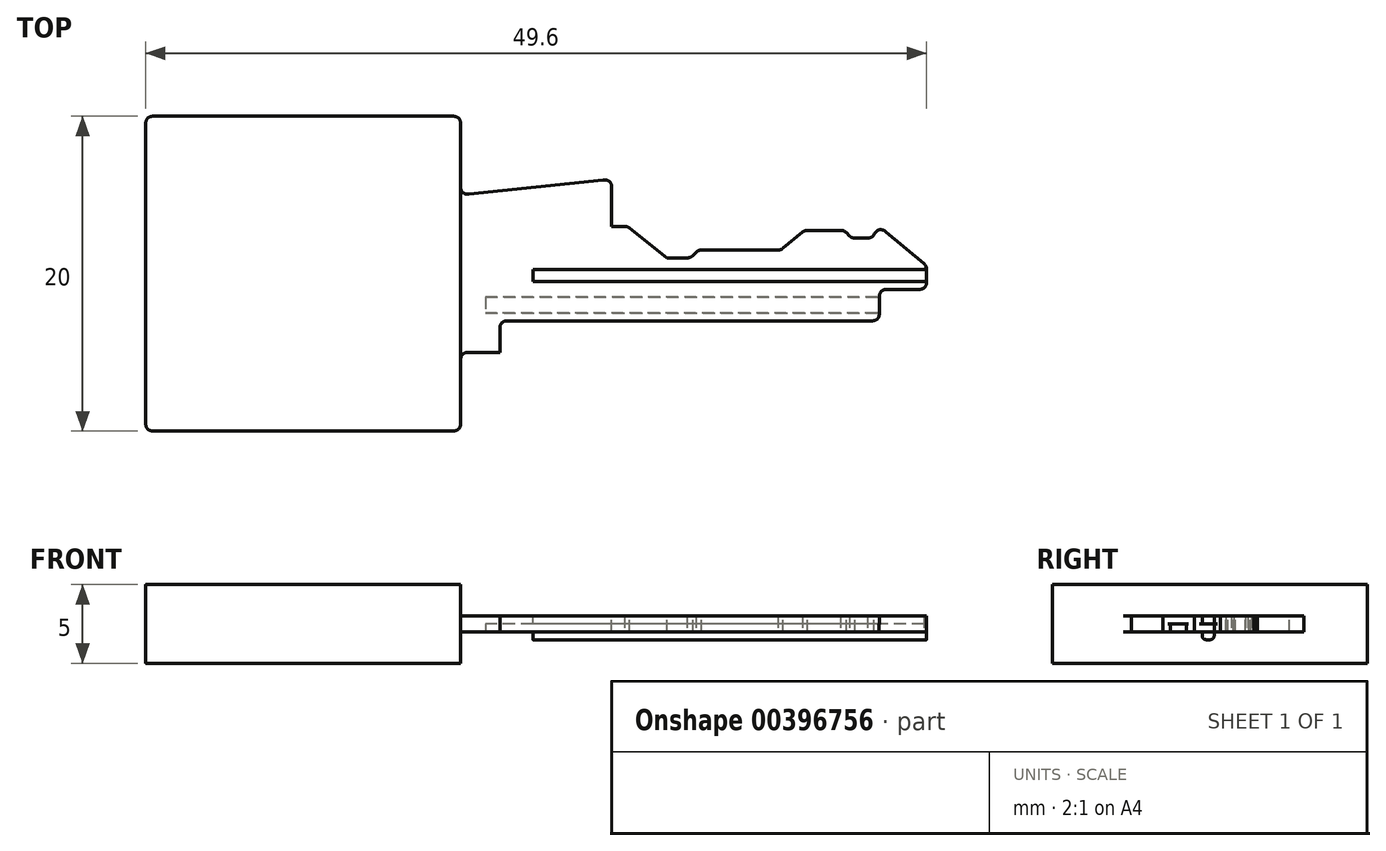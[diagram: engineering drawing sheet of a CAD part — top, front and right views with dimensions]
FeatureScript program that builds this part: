
annotation { "Feature Type Name" : "Feature", "Feature Type Description" : "" }
export const myFeature = defineFeature(function(context is Context, id is Id, definition is map)
    precondition{}
    {
        {
            var Q0;
            Q0=qCreatedBy(makeId("Top.planeOp"),FACE);
            var sketch = newSketch(context, id + "F0", { "sketchPlane" : qUnion([Q0])});
            skLineSegment(sketch, "E0.bottom", {"start": v(0, 0) * mm, "end": v(-20, 0) * mm});
            skLineSegment(sketch, "E0.top", {"start": v(0, 20) * mm, "end": v(-20, 20) * mm});
            skLineSegment(sketch, "E0.left", {"start": v(0, 0) * mm, "end": v(0, 20) * mm});
            skLineSegment(sketch, "E0.right", {"start": v(-20, 0) * mm, "end": v(-20, 20) * mm});
            skLineSegment(sketch, "E1", {"start": v(0, 15) * mm, "end": v(10, 15) * mm});
            skLineSegment(sketch, "E2", {"start": v(10, 15) * mm, "end": v(10, 5) * mm});
            skLineSegment(sketch, "E3", {"start": v(10, 5) * mm, "end": v(0, 5) * mm});
            skLineSegment(sketch, "E4", {"start": v(0, 5) * mm, "end": v(0, 15) * mm});
            skLineSegment(sketch, "E5.bottom", {"start": v(10, 15) * mm, "end": v(39, 15) * mm});
            skLineSegment(sketch, "E5.top", {"start": v(10, 5) * mm, "end": v(39, 5) * mm});
            skLineSegment(sketch, "E5.right", {"start": v(39, 15) * mm, "end": v(39, 5) * mm});
            skSolve(sketch);
        }
        {
            var Q0;
            {var subQ3=sQuery(id+"F0.wireOp",EDGE,"E0.bottom");Q0=makeQuery(id+"F0.imprint","IMPRINT",FACE,{"disambiguationData":[TD([[makeQuery(id+"F0.imprint","IMPRINT",EDGE,{"derivedFrom":subQ3}),-1.0]])]});}
            var Q1;
            Q1=makeQuery(id+"F0.imprint","IMPRINT",FACE,{"disambiguationData":[TD([[makeQuery(id+"F0.imprint","IMPRINT",EDGE,{"derivedFrom":sQuery(id+"F0.wireOp",EDGE,"E1")}),-1.0]])]});
            var Q2;
            Q2=makeQuery(id+"F0.imprint","IMPRINT",FACE,{"disambiguationData":[TD([[makeQuery(id+"F0.imprint","IMPRINT",EDGE,{"derivedFrom":sQuery(id+"F0.wireOp",EDGE,"E5.bottom")}),-1.0]])]});
            extrude(context, id + "F1", {"entities" : qUnion([Q0, Q1, Q2]), "depth" : 1 * mm});
        }
        {
            var Q0;
            Q0=makeQuery(id+"F1.opExtrude","CAP_FACE",FACE,{"disambiguationData":[OSD([sQuery(id+"F0.wireOp",EDGE,"E0.bottom"),sQuery(id+"F0.wireOp",EDGE,"E0.top"),sQuery(id+"F0.wireOp",EDGE,"E0.left"),sQuery(id+"F0.wireOp",EDGE,"E0.right"),sQuery(id+"F0.wireOp",EDGE,"E1"),sQuery(id+"F0.wireOp",EDGE,"E3"),sQuery(id+"F0.wireOp",EDGE,"E5.bottom"),sQuery(id+"F0.wireOp",EDGE,"E5.top"),sQuery(id+"F0.wireOp",EDGE,"E5.right")])],"isStart":false});
            var sketch = newSketch(context, id + "F2", { "sketchPlane" : qUnion([Q0])});
            skLineSegment(sketch, "E6", {"start": v(0, 15) * mm, "end": v(9.6, 15) * mm});
            skLineSegment(sketch, "E7", {"start": v(9.6, 15) * mm, "end": v(9.6, 16) * mm});
            skLineSegment(sketch, "E8", {"start": v(9.6, 16) * mm, "end": v(0, 15) * mm});
            skSolve(sketch);
        }
        {
            var Q0;
            Q0=makeQuery(id+"F2.imprint","IMPRINT",FACE,{"disambiguationData":[TD([[makeQuery(id+"F2.imprint","IMPRINT",EDGE,{"derivedFrom":sQuery(id+"F2.wireOp",EDGE,"E6")}),1.0]])]});
            extrude(context, id + "F3", {"entities" : qUnion([Q0]), "operationType" : NewBodyOperationType.ADD, "oppositeDirection" : true, "depth" : 1 * mm});
        }
        {
            var Q0;
            Q0=makeQuery(id+"F3.boolean.opBoolean","MERGE",FACE,{"derivedFrom":[makeQuery(id+"F1.opExtrude","CAP_FACE",FACE,{"disambiguationData":[OSD([sQuery(id+"F0.wireOp",EDGE,"E0.bottom"),sQuery(id+"F0.wireOp",EDGE,"E0.top"),sQuery(id+"F0.wireOp",EDGE,"E0.left"),sQuery(id+"F0.wireOp",EDGE,"E0.right"),sQuery(id+"F0.wireOp",EDGE,"E1"),sQuery(id+"F0.wireOp",EDGE,"E3"),sQuery(id+"F0.wireOp",EDGE,"E5.bottom"),sQuery(id+"F0.wireOp",EDGE,"E5.top"),sQuery(id+"F0.wireOp",EDGE,"E5.right")])],"isStart":false}),makeQuery(id+"F3.opExtrude","CAP_FACE",FACE,{"disambiguationData":[OSD([sQuery(id+"F2.wireOp",EDGE,"E6"),sQuery(id+"F2.wireOp",EDGE,"E7"),sQuery(id+"F2.wireOp",EDGE,"E8")])],"isStart":true})]});
            var sketch = newSketch(context, id + "F4", { "sketchPlane" : qUnion([Q0])});
            skLineSegment(sketch, "E9", {"start": v(9.6, 15) * mm, "end": v(9.6, 13) * mm});
            skLineSegment(sketch, "E10", {"start": v(9.6, 13) * mm, "end": v(10.6, 13) * mm});
            skLineSegment(sketch, "E11", {"start": v(10.6, 13) * mm, "end": v(13.1, 11) * mm});
            skLineSegment(sketch, "E12", {"start": v(13.1, 11) * mm, "end": v(14.6, 11) * mm});
            skLineSegment(sketch, "E13", {"start": v(14.6, 11) * mm, "end": v(15.1, 11.5) * mm});
            skLineSegment(sketch, "E14", {"start": v(15.1, 11.5) * mm, "end": v(20.35, 11.5) * mm});
            skLineSegment(sketch, "E15", {"start": v(20.35, 11.5) * mm, "end": v(21.85, 12.75) * mm});
            skLineSegment(sketch, "E16", {"start": v(21.85, 12.75) * mm, "end": v(24.35, 12.75) * mm});
            skLineSegment(sketch, "E17", {"start": v(24.35, 12.75) * mm, "end": v(24.85, 12.25) * mm});
            skLineSegment(sketch, "E18", {"start": v(24.85, 12.25) * mm, "end": v(26.1, 12.25) * mm});
            skLineSegment(sketch, "E19", {"start": v(26.1, 12.25) * mm, "end": v(26.6, 13) * mm});
            skLineSegment(sketch, "E20", {"start": v(26.6, 13) * mm, "end": v(29.6, 10.5) * mm});
            skLineSegment(sketch, "E21", {"start": v(29.6, 10.5) * mm, "end": v(29.6, 9) * mm});
            skLineSegment(sketch, "E22", {"start": v(29.6, 9) * mm, "end": v(26.6, 9) * mm});
            skLineSegment(sketch, "E23", {"start": v(26.6, 9) * mm, "end": v(26.6, 7) * mm});
            skLineSegment(sketch, "E24", {"start": v(26.6, 7) * mm, "end": v(2.5, 7) * mm});
            skLineSegment(sketch, "E25", {"start": v(2.5, 7) * mm, "end": v(2.5, 5) * mm});
            skLineSegment(sketch, "E26", {"start": v(2.5, 5) * mm, "end": v(39, 5) * mm});
            skLineSegment(sketch, "E27", {"start": v(39, 5) * mm, "end": v(39, 15) * mm});
            skLineSegment(sketch, "E28", {"start": v(39, 15) * mm, "end": v(9.6, 15) * mm});
            skSolve(sketch);
        }
        {
            var Q0;
            Q0=makeQuery(id+"F4.imprint","IMPRINT",FACE,{"disambiguationData":[TD([[makeQuery(id+"F4.imprint","IMPRINT",EDGE,{"derivedFrom":sQuery(id+"F4.wireOp",EDGE,"E9")}),1.0]])]});
            extrude(context, id + "F5", {"entities" : qUnion([Q0]), "operationType" : NewBodyOperationType.REMOVE, "oppositeDirection" : true, "depth" : 1 * mm});
        }
        {
            var Q0;
            Q0=makeQuery(id+"F3.opExtrude","SWEPT_EDGE",EDGE,{"disambiguationData":[OSD([sQuery(id+"F2.wireOp",EDGE,"E7"),sQuery(id+"F2.wireOp",EDGE,"E8")])]});
            var Q1;
            Q1=makeQuery(id+"F5.boolean.opBoolean","COPY",EDGE,{"derivedFrom":makeQuery(id+"F5.opExtrude","SWEPT_EDGE",EDGE,{"disambiguationData":[OSD([sQuery(id+"F4.wireOp",EDGE,"E10"),sQuery(id+"F4.wireOp",EDGE,"E11")])]})});
            var Q2;
            Q2=makeQuery(id+"F5.boolean.opBoolean","COPY",EDGE,{"derivedFrom":makeQuery(id+"F5.opExtrude","SWEPT_EDGE",EDGE,{"disambiguationData":[OSD([sQuery(id+"F4.wireOp",EDGE,"E12"),sQuery(id+"F4.wireOp",EDGE,"E13")])]})});
            var Q3;
            Q3=makeQuery(id+"F5.boolean.opBoolean","COPY",EDGE,{"derivedFrom":makeQuery(id+"F5.opExtrude","SWEPT_EDGE",EDGE,{"disambiguationData":[OSD([sQuery(id+"F4.wireOp",EDGE,"E14"),sQuery(id+"F4.wireOp",EDGE,"E15")])]})});
            var Q4;
            Q4=makeQuery(id+"F5.boolean.opBoolean","COPY",EDGE,{"derivedFrom":makeQuery(id+"F5.opExtrude","SWEPT_EDGE",EDGE,{"disambiguationData":[OSD([sQuery(id+"F4.wireOp",EDGE,"E15"),sQuery(id+"F4.wireOp",EDGE,"E16")])]})});
            var Q5;
            Q5=makeQuery(id+"F5.boolean.opBoolean","COPY",EDGE,{"derivedFrom":makeQuery(id+"F5.opExtrude","SWEPT_EDGE",EDGE,{"disambiguationData":[OSD([sQuery(id+"F4.wireOp",EDGE,"E16"),sQuery(id+"F4.wireOp",EDGE,"E17")])]})});
            var Q6;
            Q6=makeQuery(id+"F5.boolean.opBoolean","COPY",EDGE,{"derivedFrom":makeQuery(id+"F5.opExtrude","SWEPT_EDGE",EDGE,{"disambiguationData":[OSD([sQuery(id+"F4.wireOp",EDGE,"E17"),sQuery(id+"F4.wireOp",EDGE,"E18")])]})});
            var Q7;
            Q7=makeQuery(id+"F5.boolean.opBoolean","COPY",EDGE,{"derivedFrom":makeQuery(id+"F5.opExtrude","SWEPT_EDGE",EDGE,{"disambiguationData":[OSD([sQuery(id+"F4.wireOp",EDGE,"E18"),sQuery(id+"F4.wireOp",EDGE,"E19")])]})});
            var Q8;
            Q8=makeQuery(id+"F5.boolean.opBoolean","COPY",EDGE,{"derivedFrom":makeQuery(id+"F5.opExtrude","SWEPT_EDGE",EDGE,{"disambiguationData":[OSD([sQuery(id+"F4.wireOp",EDGE,"E21"),sQuery(id+"F4.wireOp",EDGE,"E22")])]})});
            var Q9;
            Q9=makeQuery(id+"F5.boolean.opBoolean","COPY",EDGE,{"derivedFrom":makeQuery(id+"F5.opExtrude","SWEPT_EDGE",EDGE,{"disambiguationData":[OSD([sQuery(id+"F4.wireOp",EDGE,"E20"),sQuery(id+"F4.wireOp",EDGE,"E21")])]})});
            var Q10;
            Q10=makeQuery(id+"F5.boolean.opBoolean","COPY",EDGE,{"derivedFrom":makeQuery(id+"F5.opExtrude","SWEPT_EDGE",EDGE,{"disambiguationData":[OSD([sQuery(id+"F4.wireOp",EDGE,"E19"),sQuery(id+"F4.wireOp",EDGE,"E20")])]})});
            var Q11;
            Q11=makeQuery(id+"F5.boolean.opBoolean","COPY",EDGE,{"derivedFrom":makeQuery(id+"F5.opExtrude","SWEPT_EDGE",EDGE,{"disambiguationData":[OSD([sQuery(id+"F4.wireOp",EDGE,"E22"),sQuery(id+"F4.wireOp",EDGE,"E23")])]})});
            var Q12;
            Q12=makeQuery(id+"F5.boolean.opBoolean","COPY",EDGE,{"derivedFrom":makeQuery(id+"F5.opExtrude","SWEPT_EDGE",EDGE,{"disambiguationData":[OSD([sQuery(id+"F4.wireOp",EDGE,"E23"),sQuery(id+"F4.wireOp",EDGE,"E24")])]})});
            var Q13;
            Q13=makeQuery(id+"F5.boolean.opBoolean","COPY",EDGE,{"derivedFrom":makeQuery(id+"F5.opExtrude","SWEPT_EDGE",EDGE,{"disambiguationData":[OSD([sQuery(id+"F4.wireOp",EDGE,"E24"),sQuery(id+"F4.wireOp",EDGE,"E25")])]})});
            var Q14;
            Q14=makeQuery(id+"F5.boolean.opBoolean","COPY",EDGE,{"derivedFrom":makeQuery(id+"F5.opExtrude","SWEPT_EDGE",EDGE,{"disambiguationData":[OSD([sQuery(id+"F0.wireOp",EDGE,"E3"),sQuery(id+"F0.wireOp",EDGE,"E5.top"),sQuery(id+"F4.wireOp",EDGE,"E25"),sQuery(id+"F4.wireOp",EDGE,"E26")])]})});
            var Q15;
            Q15=makeQuery(id+"F1.opExtrude","SWEPT_EDGE",EDGE,{"disambiguationData":[OSD([sQuery(id+"F0.wireOp",EDGE,"E0.left"),sQuery(id+"F0.wireOp",EDGE,"E3"),sQuery(id+"F0.wireOp",EDGE,"E4")])]});
            var Q16;
            Q16=makeQuery(id+"F1.opExtrude","SWEPT_EDGE",EDGE,{"disambiguationData":[OSD([sQuery(id+"F0.wireOp",EDGE,"E0.bottom"),sQuery(id+"F0.wireOp",EDGE,"E0.left")])]});
            var Q17;
            Q17=makeQuery(id+"F1.opExtrude","SWEPT_EDGE",EDGE,{"disambiguationData":[OSD([sQuery(id+"F0.wireOp",EDGE,"E0.top"),sQuery(id+"F0.wireOp",EDGE,"E0.left")])]});
            var Q18;
            {var subQ0=sQuery(id+"F0.wireOp",EDGE,"E0.left");Q18=makeQuery(id+"F3.boolean.opBoolean","MERGE",EDGE,{"derivedFrom":[makeQuery(id+"F1.opExtrude","SWEPT_EDGE",EDGE,{"disambiguationData":[OSD([subQ0,sQuery(id+"F0.wireOp",EDGE,"E1"),sQuery(id+"F0.wireOp",EDGE,"E4")])]}),makeQuery(id+"F3.opExtrude","SWEPT_EDGE",EDGE,{"disambiguationData":[OSD([subQ0,sQuery(id+"F2.wireOp",EDGE,"E6"),sQuery(id+"F2.wireOp",EDGE,"E8")])]})]});}
            var Q19;
            Q19=makeQuery(id+"F1.opExtrude","SWEPT_EDGE",EDGE,{"disambiguationData":[OSD([sQuery(id+"F0.wireOp",EDGE,"E0.top"),sQuery(id+"F0.wireOp",EDGE,"E0.right")])]});
            var Q20;
            Q20=makeQuery(id+"F1.opExtrude","SWEPT_EDGE",EDGE,{"disambiguationData":[OSD([sQuery(id+"F0.wireOp",EDGE,"E0.bottom"),sQuery(id+"F0.wireOp",EDGE,"E0.right")])]});
            var Q21;
            Q21=makeQuery(id+"F5.boolean.opBoolean","COPY",EDGE,{"derivedFrom":makeQuery(id+"F5.opExtrude","SWEPT_EDGE",EDGE,{"disambiguationData":[OSD([sQuery(id+"F4.wireOp",EDGE,"E13"),sQuery(id+"F4.wireOp",EDGE,"E14")])]})});
            fillet(context, id + "F6", {"entities" : qUnion([Q0, Q1, Q2, Q3, Q4, Q5, Q6, Q7, Q8, Q9, Q10, Q11, Q12, Q13, Q14, Q15, Q16, Q17, Q18, Q19, Q20, Q21]), "radius" : .5 * mm, "tangentPropagation" : true, "rho" : 0.5, "crossSection" : FilletCrossSection.CONIC, "allowEdgeOverflow" : false});
        }
        {
            var Q0;
            Q0=makeQuery(id+"F5.boolean.opBoolean","COPY",FACE,{"derivedFrom":makeQuery(id+"F5.opExtrude","SWEPT_FACE",FACE,{"disambiguationData":[OSD([sQuery(id+"F4.wireOp",EDGE,"E23")])]})});
            var sketch = newSketch(context, id + "F7", { "sketchPlane" : qUnion([Q0])});
            skLineSegment(sketch, "E29", {"start": v(9, 0) * mm, "end": v(9, 0.5) * mm});
            skLineSegment(sketch, "E30", {"start": v(9, 0.5) * mm, "end": v(7.5, 0.5) * mm});
            skLineSegment(sketch, "E31", {"start": v(7.5, 0.5) * mm, "end": v(7.5, 0) * mm});
            skLineSegment(sketch, "E32", {"start": v(7.5, 0) * mm, "end": v(9, 0) * mm});
            skLineSegment(sketch, "E33", {"start": v(9, 0.5) * mm, "end": v(9, 0) * mm});
            skLineSegment(sketch, "E34", {"start": v(7.5, 1) * mm, "end": v(7.5, 1.5) * mm});
            skLineSegment(sketch, "E35", {"start": v(7.5, 1.5) * mm, "end": v(9, 1.5) * mm});
            skLineSegment(sketch, "E36", {"start": v(9, 1.5) * mm, "end": v(9, 1) * mm});
            skLineSegment(sketch, "E37", {"start": v(9, 1) * mm, "end": v(7.5, 1) * mm});
            skSolve(sketch);
        }
        {
            var Q0;
            {var subQ0=sQuery(id+"F7.wireOp",EDGE,"E31");Q0=makeQuery(id+"F7.imprint","IMPRINT",FACE,{"disambiguationData":[TD([[makeQuery(id+"F7.imprint","IMPRINT",EDGE,{"derivedFrom":subQ0}),1.0]])]});}
            extrude(context, id + "F8", {"entities" : qUnion([Q0]), "operationType" : NewBodyOperationType.REMOVE, "oppositeDirection" : true, "depth" : 25 * mm});
        }
        {
            var Q0;
            {var subQ0=sQuery(id+"F4.wireOp",EDGE,"E23");Q0=makeQuery(id+"F8.boolean.opBoolean","MERGE",EDGE,{"derivedFrom":[makeQuery(id+"F6.opFillet","BLEND_EDGE",EDGE,{"blendedFrom":[makeQuery(id+"F5.boolean.opBoolean","COPY",EDGE,{"derivedFrom":makeQuery(id+"F5.opExtrude","SWEPT_EDGE",EDGE,{"disambiguationData":[OSD([subQ0,sQuery(id+"F4.wireOp",EDGE,"E24")])]})}),makeQuery(id+"F5.boolean.opBoolean","COPY",FACE,{"derivedFrom":makeQuery(id+"F5.opExtrude","SWEPT_FACE",FACE,{"disambiguationData":[OSD([subQ0])]})})],"blendedInto":[makeQuery(id+"F5.boolean.opBoolean","COPY",FACE,{"derivedFrom":makeQuery(id+"F5.opExtrude","SWEPT_FACE",FACE,{"disambiguationData":[OSD([subQ0])]})})]}),makeQuery(id+"F8.opExtrude","CAP_EDGE",EDGE,{"disambiguationData":[OSD([sQuery(id+"F7.wireOp",EDGE,"E31")])],"isStart":true})]});}
            var Q1;
            {var subQ0=sQuery(id+"F4.wireOp",EDGE,"E23");var subQ1=sQuery(id+"F4.wireOp",EDGE,"E22");Q1=makeQuery(id+"F8.boolean.opBoolean","MERGE",EDGE,{"derivedFrom":[makeQuery(id+"F6.opFillet","BLEND_EDGE",EDGE,{"blendedFrom":[makeQuery(id+"F5.boolean.opBoolean","COPY",EDGE,{"derivedFrom":makeQuery(id+"F5.opExtrude","SWEPT_EDGE",EDGE,{"disambiguationData":[OSD([subQ1,subQ0])]})}),makeQuery(id+"F5.boolean.opBoolean","COPY",FACE,{"derivedFrom":makeQuery(id+"F5.opExtrude","SWEPT_FACE",FACE,{"disambiguationData":[OSD([subQ0])]})})],"blendedInto":[makeQuery(id+"F5.boolean.opBoolean","COPY",FACE,{"derivedFrom":makeQuery(id+"F5.opExtrude","SWEPT_FACE",FACE,{"disambiguationData":[OSD([subQ0])]})})]}),makeQuery(id+"F8.opExtrude","CAP_EDGE",EDGE,{"disambiguationData":[OSD([subQ1,subQ0])],"isStart":true})]});}
            fillet(context, id + "F9", {"entities" : qUnion([Q0, Q1]), "radius" : 0.15 * mm, "tangentPropagation" : true, "allowEdgeOverflow" : false});
        }
        {
            var Q0;
            Q0=makeQuery(id+"F5.boolean.opBoolean","COPY",FACE,{"derivedFrom":makeQuery(id+"F5.opExtrude","SWEPT_FACE",FACE,{"disambiguationData":[OSD([sQuery(id+"F4.wireOp",EDGE,"E21")])]})});
            var sketch = newSketch(context, id + "F10", { "sketchPlane" : qUnion([Q0])});
            skLineSegment(sketch, "E38", {"start": v(9.5, 1) * mm, "end": v(9.5, 0.5) * mm});
            skLineSegment(sketch, "E39", {"start": v(9.5, 0.5) * mm, "end": v(10.27, 0.5) * mm});
            skLineSegment(sketch, "E40", {"start": v(10.27, 0.5) * mm, "end": v(10.27, 1) * mm});
            skLineSegment(sketch, "E41", {"start": v(10.27, 1) * mm, "end": v(9.5, 1) * mm});
            skSolve(sketch);
        }
        {
            var Q0;
            Q0=makeQuery(id+"F10.imprint","IMPRINT",FACE,{"disambiguationData":[TD([[makeQuery(id+"F10.imprint","IMPRINT",EDGE,{"derivedFrom":sQuery(id+"F10.wireOp",EDGE,"E38")}),1.0]])]});
            extrude(context, id + "F11", {"entities" : qUnion([Q0]), "operationType" : NewBodyOperationType.REMOVE, "oppositeDirection" : true, "depth" : 25 * mm});
        }
        {
            var Q0;
            {var subQ0=sQuery(id+"F4.wireOp",EDGE,"E21");Q0=makeQuery(id+"F11.boolean.opBoolean","MERGE",EDGE,{"derivedFrom":[makeQuery(id+"F6.opFillet","BLEND_EDGE",EDGE,{"blendedFrom":[makeQuery(id+"F5.boolean.opBoolean","COPY",EDGE,{"derivedFrom":makeQuery(id+"F5.opExtrude","SWEPT_EDGE",EDGE,{"disambiguationData":[OSD([subQ0,sQuery(id+"F4.wireOp",EDGE,"E22")])]})}),makeQuery(id+"F5.boolean.opBoolean","COPY",FACE,{"derivedFrom":makeQuery(id+"F5.opExtrude","SWEPT_FACE",FACE,{"disambiguationData":[OSD([subQ0])]})})],"blendedInto":[makeQuery(id+"F5.boolean.opBoolean","COPY",FACE,{"derivedFrom":makeQuery(id+"F5.opExtrude","SWEPT_FACE",FACE,{"disambiguationData":[OSD([subQ0])]})})]}),makeQuery(id+"F11.opExtrude","CAP_EDGE",EDGE,{"disambiguationData":[OSD([sQuery(id+"F10.wireOp",EDGE,"E38")])],"isStart":true})]});}
            var Q1;
            {var subQ0=sQuery(id+"F4.wireOp",EDGE,"E21");Q1=makeQuery(id+"F11.boolean.opBoolean","MERGE",EDGE,{"derivedFrom":[makeQuery(id+"F6.opFillet","BLEND_EDGE",EDGE,{"blendedFrom":[makeQuery(id+"F5.boolean.opBoolean","COPY",EDGE,{"derivedFrom":makeQuery(id+"F5.opExtrude","SWEPT_EDGE",EDGE,{"disambiguationData":[OSD([sQuery(id+"F4.wireOp",EDGE,"E20"),subQ0])]})}),makeQuery(id+"F5.boolean.opBoolean","COPY",FACE,{"derivedFrom":makeQuery(id+"F5.opExtrude","SWEPT_FACE",FACE,{"disambiguationData":[OSD([subQ0])]})})],"blendedInto":[makeQuery(id+"F5.boolean.opBoolean","COPY",FACE,{"derivedFrom":makeQuery(id+"F5.opExtrude","SWEPT_FACE",FACE,{"disambiguationData":[OSD([subQ0])]})})]}),makeQuery(id+"F11.opExtrude","CAP_EDGE",EDGE,{"disambiguationData":[OSD([sQuery(id+"F10.wireOp",EDGE,"E40")])],"isStart":true})]});}
            fillet(context, id + "F12", {"entities" : qUnion([Q0, Q1]), "radius" : .15 * mm, "tangentPropagation" : true, "allowEdgeOverflow" : false});
        }
        {
            var Q0;
            Q0=makeQuery(id+"F5.boolean.opBoolean","COPY",FACE,{"derivedFrom":makeQuery(id+"F5.opExtrude","SWEPT_FACE",FACE,{"disambiguationData":[OSD([sQuery(id+"F4.wireOp",EDGE,"E21")])]})});
            var sketch = newSketch(context, id + "F13", { "sketchPlane" : qUnion([Q0])});
            skLineSegment(sketch, "E42", {"start": v(9.5, 0) * mm, "end": v(9.5, -0.5) * mm});
            skLineSegment(sketch, "E43", {"start": v(9.5, -0.5) * mm, "end": v(10.27, -0.5) * mm});
            skLineSegment(sketch, "E44", {"start": v(10.27, -0.5) * mm, "end": v(10.27, 0) * mm});
            skSolve(sketch);
        }
        {
            var Q0;
            Q0=makeQuery(id+"F13.imprint","IMPRINT",FACE,{"disambiguationData":[TD([[makeQuery(id+"F13.imprint","IMPRINT",EDGE,{"derivedFrom":sQuery(id+"F13.wireOp",EDGE,"E42")}),1.0]])]});
            extrude(context, id + "F14", {"entities" : qUnion([Q0]), "oppositeDirection" : true, "depth" : 25 * mm});
        }
        {
            var Q0;
            Q0=makeQuery(id+"F14.opExtrude","SWEPT_EDGE",EDGE,{"disambiguationData":[OSD([sQuery(id+"F13.wireOp",EDGE,"E42"),sQuery(id+"F13.wireOp",EDGE,"E43")])]});
            var Q1;
            Q1=makeQuery(id+"F14.opExtrude","SWEPT_EDGE",EDGE,{"disambiguationData":[OSD([sQuery(id+"F13.wireOp",EDGE,"E43"),sQuery(id+"F13.wireOp",EDGE,"E44")])]});
            fillet(context, id + "F15", {"entities" : qUnion([Q0, Q1]), "radius" : .25 * mm, "tangentPropagation" : true, "allowEdgeOverflow" : false});
        }
        {
            var Q0;
            Q0=makeQuery(id+"F3.boolean.opBoolean","MERGE",FACE,{"derivedFrom":[makeQuery(id+"F1.opExtrude","CAP_FACE",FACE,{"disambiguationData":[OSD([sQuery(id+"F0.wireOp",EDGE,"E0.bottom"),sQuery(id+"F0.wireOp",EDGE,"E0.top"),sQuery(id+"F0.wireOp",EDGE,"E0.left"),sQuery(id+"F0.wireOp",EDGE,"E0.right"),sQuery(id+"F0.wireOp",EDGE,"E1"),sQuery(id+"F0.wireOp",EDGE,"E3"),sQuery(id+"F0.wireOp",EDGE,"E5.bottom"),sQuery(id+"F0.wireOp",EDGE,"E5.top"),sQuery(id+"F0.wireOp",EDGE,"E5.right")])],"isStart":false}),makeQuery(id+"F3.opExtrude","CAP_FACE",FACE,{"disambiguationData":[OSD([sQuery(id+"F2.wireOp",EDGE,"E6"),sQuery(id+"F2.wireOp",EDGE,"E7"),sQuery(id+"F2.wireOp",EDGE,"E8")])],"isStart":true})]});
            var sketch = newSketch(context, id + "F16", { "sketchPlane" : qUnion([Q0])});
            skLineSegment(sketch, "E45", {"start": v(0, 0) * mm, "end": v(-20, 0) * mm});
            skLineSegment(sketch, "E46", {"start": v(-20, 0) * mm, "end": v(-20, 19.5) * mm});
            skLineSegment(sketch, "E47", {"start": v(-20, 19.5) * mm, "end": v(-20, 20) * mm});
            skLineSegment(sketch, "E48", {"start": v(-20, 20) * mm, "end": v(0, 20) * mm});
            skLineSegment(sketch, "E49", {"start": v(0, 20) * mm, "end": v(0, 0) * mm});
            skSolve(sketch);
        }
        {
            var Q0;
            {var subQ1=sQuery(id+"F2.wireOp",EDGE,"E8");var subQ2=sQuery(id+"F2.wireOp",EDGE,"E6");var subQ3=sQuery(id+"F0.wireOp",EDGE,"E3");var subQ4=sQuery(id+"F0.wireOp",EDGE,"E1");var subQ5=sQuery(id+"F0.wireOp",EDGE,"E0.right");var subQ6=sQuery(id+"F0.wireOp",EDGE,"E0.left");var subQ7=sQuery(id+"F0.wireOp",EDGE,"E0.top");var subQ8=sQuery(id+"F0.wireOp",EDGE,"E0.bottom");var subQ9=makeQuery(id+"F3.boolean.opBoolean","MERGE",FACE,{"derivedFrom":[makeQuery(id+"F1.opExtrude","CAP_FACE",FACE,{"disambiguationData":[OSD([subQ8,subQ7,subQ6,subQ5,subQ4,subQ3,sQuery(id+"F0.wireOp",EDGE,"E5.bottom"),sQuery(id+"F0.wireOp",EDGE,"E5.top"),sQuery(id+"F0.wireOp",EDGE,"E5.right")])],"isStart":false}),makeQuery(id+"F3.opExtrude","CAP_FACE",FACE,{"disambiguationData":[OSD([subQ2,sQuery(id+"F2.wireOp",EDGE,"E7"),subQ1])],"isStart":true})]});var subQ15=makeQuery(id+"F6.opFillet","BLEND_EDGE",EDGE,{"blendedFrom":[makeQuery(id+"F1.opExtrude","SWEPT_EDGE",EDGE,{"disambiguationData":[OSD([subQ8,subQ6])]}),subQ9],"blendedInto":[subQ9]});Q0=makeQuery(id+"F16.imprint","IMPRINT",FACE,{"disambiguationData":[TD([[makeQuery(id+"F16.imprint","IMPRINT",EDGE,{"derivedFrom":subQ15}),1.0]])]});}
            extrude(context, id + "F17", {"entities" : qUnion([Q0]), "operationType" : NewBodyOperationType.ADD, "depth" : 2 * mm});
        }
        {
            var Q0;
            Q0=makeQuery(id+"F3.boolean.opBoolean","MERGE",FACE,{"derivedFrom":[makeQuery(id+"F1.opExtrude","CAP_FACE",FACE,{"disambiguationData":[OSD([sQuery(id+"F0.wireOp",EDGE,"E0.bottom"),sQuery(id+"F0.wireOp",EDGE,"E0.top"),sQuery(id+"F0.wireOp",EDGE,"E0.left"),sQuery(id+"F0.wireOp",EDGE,"E0.right"),sQuery(id+"F0.wireOp",EDGE,"E1"),sQuery(id+"F0.wireOp",EDGE,"E3"),sQuery(id+"F0.wireOp",EDGE,"E5.bottom"),sQuery(id+"F0.wireOp",EDGE,"E5.top"),sQuery(id+"F0.wireOp",EDGE,"E5.right")])],"isStart":true}),makeQuery(id+"F3.opExtrude","CAP_FACE",FACE,{"disambiguationData":[OSD([sQuery(id+"F2.wireOp",EDGE,"E6"),sQuery(id+"F2.wireOp",EDGE,"E7"),sQuery(id+"F2.wireOp",EDGE,"E8")])],"isStart":false})]});
            var sketch = newSketch(context, id + "F18", { "sketchPlane" : qUnion([Q0])});
            skLineSegment(sketch, "E50", {"start": v(-20, 0) * mm, "end": v(-20, -20) * mm});
            skLineSegment(sketch, "E51", {"start": v(-20, -20) * mm, "end": v(0, -20) * mm});
            skLineSegment(sketch, "E52", {"start": v(0, -20) * mm, "end": v(0, 0) * mm});
            skLineSegment(sketch, "E53", {"start": v(0, 0) * mm, "end": v(-20, 0) * mm});
            skSolve(sketch);
        }
        {
            var Q0;
            {var subQ1=sQuery(id+"F2.wireOp",EDGE,"E8");var subQ2=sQuery(id+"F2.wireOp",EDGE,"E6");var subQ3=sQuery(id+"F0.wireOp",EDGE,"E3");var subQ4=sQuery(id+"F0.wireOp",EDGE,"E1");var subQ5=sQuery(id+"F0.wireOp",EDGE,"E0.right");var subQ6=sQuery(id+"F0.wireOp",EDGE,"E0.left");var subQ7=sQuery(id+"F0.wireOp",EDGE,"E0.top");var subQ8=sQuery(id+"F0.wireOp",EDGE,"E0.bottom");var subQ9=makeQuery(id+"F3.boolean.opBoolean","MERGE",FACE,{"derivedFrom":[makeQuery(id+"F1.opExtrude","CAP_FACE",FACE,{"disambiguationData":[OSD([subQ8,subQ7,subQ6,subQ5,subQ4,subQ3,sQuery(id+"F0.wireOp",EDGE,"E5.bottom"),sQuery(id+"F0.wireOp",EDGE,"E5.top"),sQuery(id+"F0.wireOp",EDGE,"E5.right")])],"isStart":true}),makeQuery(id+"F3.opExtrude","CAP_FACE",FACE,{"disambiguationData":[OSD([subQ2,sQuery(id+"F2.wireOp",EDGE,"E7"),subQ1])],"isStart":false})]});var subQ10=makeQuery(id+"F6.opFillet","BLEND_EDGE",EDGE,{"blendedFrom":[makeQuery(id+"F1.opExtrude","SWEPT_EDGE",EDGE,{"disambiguationData":[OSD([subQ8,subQ6])]}),subQ9],"blendedInto":[subQ9]});Q0=makeQuery(id+"F18.imprint","IMPRINT",FACE,{"disambiguationData":[TD([[makeQuery(id+"F18.imprint","IMPRINT",EDGE,{"derivedFrom":subQ10}),1.0]])]});}
            extrude(context, id + "F19", {"entities" : qUnion([Q0]), "operationType" : NewBodyOperationType.ADD, "depth" : 2 * mm});
        }
    });
